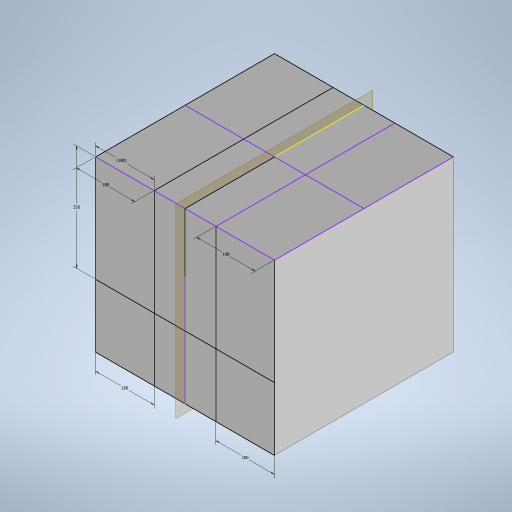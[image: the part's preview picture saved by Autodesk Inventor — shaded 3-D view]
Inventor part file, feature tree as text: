
AUTODESK INVENTOR PART (.ipt)
format: ipt  version: 2024 (Build 280153000, 153)  size: 12,787,712 bytes
history: native  units: mm
features: other x6, sketch x4, plane x2, extrude x1
ambient origin geometry x8: Origin, YZ Plane, XZ Plane, XY Plane, X Axis, Y Axis, Z Axis, Center Point
bodies: Body1 (feature_tree)
feature tree (13):
  other  "M.ipt"
  plane  "Plano de trabajo1"
  extrude  "Extrusión1"  [1 undecoded]
  other  "Combinar1"
  sketch  "Boceto3"  dims[d2=550.0mm]
  sketch  "Boceto4"  dims[d3=520.0mm]
  plane  "Plano de trabajo2"
  sketch  "Boceto5"  dims[d4=550.0mm d5=0.0mm d6=129.8482mm d17=180.0mm d18=180.0mm d22=326.0mm d23=180.0mm d24=180.0mm d25=180.0mm d14=0.5mm d15=0.872665mm d16=0.5mm d19=0.5mm d20=0.872665mm d21=0.5mm d26=0.5mm d27=0.872665mm d28=0.5mm d29=0.872665mm]
  other  "Sólido1::M.ipt"
  other  "OperaciónIdentificador1"
  sketch  "Boceto1"  dims[d0=25.0mm d1=-365.0mm]
  other  "Sólido2"
  other  "Sólido1"
note: 1 required parameter value undecoded (feature->parameter linkage not recoverable at this tier; creation-order binding heuristic only, values carry confidence <= 0.55)
